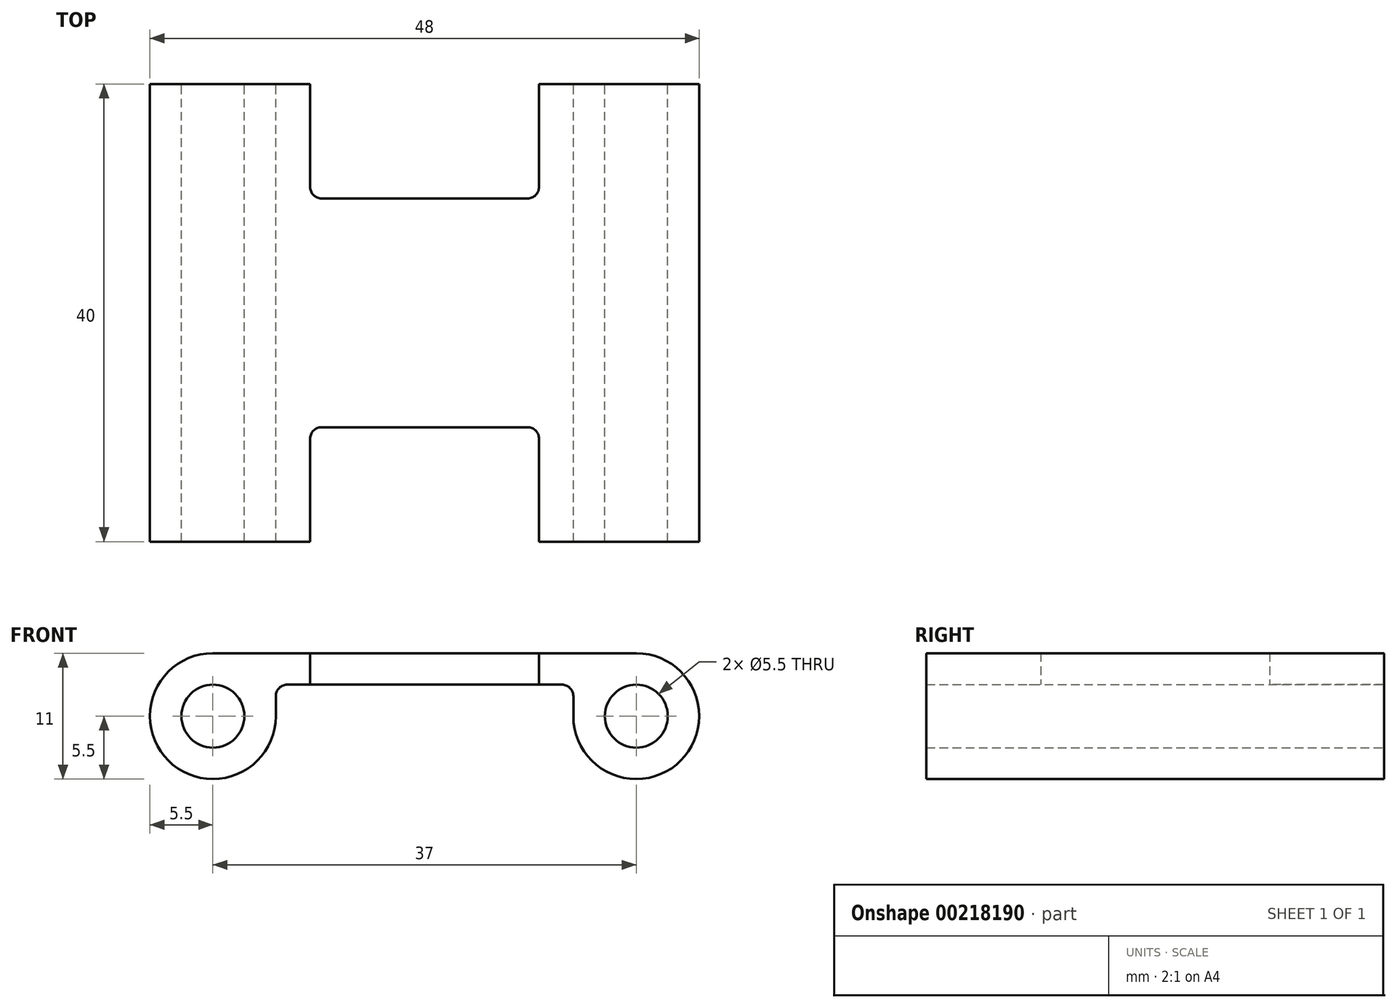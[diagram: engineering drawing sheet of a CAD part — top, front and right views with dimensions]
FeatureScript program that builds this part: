
annotation { "Feature Type Name" : "Feature", "Feature Type Description" : "" }
export const myFeature = defineFeature(function(context is Context, id is Id, definition is map)
    precondition{}
    {
        {
            var Q0;
            Q0=qCreatedBy(makeId("Front.planeOp"),FACE);
            var sketch = newSketch(context, id + "F0", { "sketchPlane" : qUnion([Q0])});
            skLineSegment(sketch, "E0", {"start": v(0, 5.5) * mm, "end": v(37, 5.5) * mm});
            skLineSegment(sketch, "E1", {"start": v(6.5, 2.75) * mm, "end": v(30.5, 2.75) * mm});
            skLineSegment(sketch, "E2", {"start": v(5.5, 0) * mm, "end": v(5.5, 1.75) * mm});
            skLineSegment(sketch, "E3", {"start": v(31.5, 0) * mm, "end": v(31.5, 1.75) * mm});
            skPoint(sketch, "E4.orphan", {"position": v(0, 2.75) * mm});
            skPoint(sketch, "E5.visualSharp", {"position": v(5.5, 2.75) * mm});
            skArc(sketch, "E5.filletArc", {"start": v(6.5, 2.75) * mm, "mid": v(5.8, 2.46) * mm, "end": v(5.5, 1.75) * mm});
            skPoint(sketch, "E6.visualSharp", {"position": v(31.5, 2.75) * mm});
            skArc(sketch, "E6.filletArc", {"start": v(31.5, 1.75) * mm, "mid": v(31.2, 2.46) * mm, "end": v(30.5, 2.75) * mm});
            skPoint(sketch, "E7.visualSharp", {"position": v(5.5, 0) * mm});
            skPoint(sketch, "E8.visualSharp", {"position": v(31.5, 0) * mm});
            skCircle(sketch, "E9", {"center": v(37, 0) * mm, "radius": 2.75 * mm});
            skCircle(sketch, "E10", {"center": v(0, 0) * mm, "radius": 2.75 * mm});
            skArc(sketch, "E11", {"start": v(31.5, 0) * mm, "mid": v(40.89, -3.89) * mm, "end": v(37, 5.5) * mm});
            skArc(sketch, "E12", {"start": v(0, 5.5) * mm, "mid": v(-3.89, -3.89) * mm, "end": v(5.5, 0) * mm});
            skSolve(sketch);
        }
        {
            var Q0;
            Q0=qSketchRegion(id+"F0",true);
            extrude(context, id + "F1", {"entities" : qUnion([Q0]), "depth" : 20 * mm, "hasSecondDirection" : true, "secondDirectionOppositeDirection" : true, "secondDirectionDepth" : 20 * mm});
        }
        {
            var Q0;
            {var subQ2=sQuery(id+"F0.wireOp",EDGE,"E1");Q0=makeQuery(id+"FyGTzeMTxIq73NX_1.boolean.opBoolean","SPLIT",FACE,{"disambiguationData":[TD([makeQuery(id+"FyGTzeMTxIq73NX_1.opExtrude","SWEPT_FACE",FACE,{"disambiguationData":[OSD([sQuery(id+"FarfYcdUMCQoenl_1.wireOp",EDGE,"kt06CgWY-HaNg-SO35-Ci6H-CknEjbLrrtwM.bottom")])]})])],"derivedFrom":makeQuery(id+"F1.opExtrude","SWEPT_FACE",FACE,{"disambiguationData":[OSD([subQ2])]})});}
            var sketch = newSketch(context, id + "F2", { "sketchPlane" : qUnion([Q0])});
            skLineSegment(sketch, "E13", {"start": v(18.5, -20) * mm, "end": v(18.5, 20.03) * mm, "construction": true});
            skLineSegment(sketch, "E14.bottom", {"start": v(8.5, -20) * mm, "end": v(28.5, -20) * mm});
            skLineSegment(sketch, "E14.top", {"start": v(8.5, -10) * mm, "end": v(28.5, -10) * mm});
            skLineSegment(sketch, "E14.left", {"start": v(8.5, -20) * mm, "end": v(8.5, -10) * mm});
            skLineSegment(sketch, "E14.right", {"start": v(28.5, -20) * mm, "end": v(28.5, -10) * mm});
            skLineSegment(sketch, "E15.bottom", {"start": v(8.5, 20) * mm, "end": v(28.5, 20) * mm});
            skLineSegment(sketch, "E15.top", {"start": v(8.5, 10) * mm, "end": v(28.5, 10) * mm});
            skLineSegment(sketch, "E15.left", {"start": v(8.5, 20) * mm, "end": v(8.5, 10) * mm});
            skLineSegment(sketch, "E15.right", {"start": v(28.5, 20) * mm, "end": v(28.5, 10) * mm});
            skLineSegment(sketch, "E16", {"start": v(-5.61, 0) * mm, "end": v(43.07, 0) * mm, "construction": true});
            skSolve(sketch);
        }
        {
            var Q0;
            Q0=qSketchRegion(id+"F2",true);
            extrude(context, id + "F3", {"entities" : qUnion([Q0]), "operationType" : NewBodyOperationType.REMOVE, "endBound" : BoundingType.UP_TO_NEXT, "oppositeDirection" : true, "depth" : 25 * mm});
        }
        {
            var Q0;
            Q0=makeQuery(id+"F3.boolean.opBoolean","COPY",EDGE,{"derivedFrom":makeQuery(id+"F3.opExtrude","CAP_EDGE",EDGE,{"disambiguationData":[OSD([sQuery(id+"F2.wireOp",EDGE,"E15.left")])],"isStart":true})});
            var Q1;
            Q1=makeQuery(id+"F3.boolean.opBoolean","COPY",EDGE,{"derivedFrom":makeQuery(id+"F3.opExtrude","CAP_EDGE",EDGE,{"disambiguationData":[OSD([sQuery(id+"F2.wireOp",EDGE,"E14.left")])],"isStart":true})});
            var Q2;
            Q2=makeQuery(id+"F3.boolean.opBoolean","COPY",EDGE,{"derivedFrom":makeQuery(id+"F3.opExtrude","CAP_EDGE",EDGE,{"disambiguationData":[OSD([sQuery(id+"F2.wireOp",EDGE,"E14.right")])],"isStart":true})});
            var Q3;
            Q3=makeQuery(id+"F3.boolean.opBoolean","COPY",EDGE,{"derivedFrom":makeQuery(id+"F3.opExtrude","CAP_EDGE",EDGE,{"disambiguationData":[OSD([sQuery(id+"F2.wireOp",EDGE,"E15.right")])],"isStart":true})});
            var Q4;
            Q4=makeQuery(id+"FyGTzeMTxIq73NX_1.opExtrude","CAP_EDGE",EDGE,{"disambiguationData":[OSD([sQuery(id+"FarfYcdUMCQoenl_1.wireOp",EDGE,"kt06CgWY-HaNg-SO35-Ci6H-CknEjbLrrtwM.top")])],"isStart":true});
            var Q5;
            Q5=makeQuery(id+"FyGTzeMTxIq73NX_1.opExtrude","CAP_EDGE",EDGE,{"disambiguationData":[OSD([sQuery(id+"FarfYcdUMCQoenl_1.wireOp",EDGE,"kt06CgWY-HaNg-SO35-Ci6H-CknEjbLrrtwM.bottom")])],"isStart":true});
            var Q6;
            Q6=makeQuery(id+"F3.boolean.opBoolean","COPY",EDGE,{"derivedFrom":makeQuery(id+"F3.opExtrude","SWEPT_EDGE",EDGE,{"disambiguationData":[OSD([sQuery(id+"F2.wireOp",EDGE,"E15.top"),sQuery(id+"F2.wireOp",EDGE,"E15.left")])]})});
            var Q7;
            Q7=makeQuery(id+"F3.boolean.opBoolean","COPY",EDGE,{"derivedFrom":makeQuery(id+"F3.opExtrude","SWEPT_EDGE",EDGE,{"disambiguationData":[OSD([sQuery(id+"F2.wireOp",EDGE,"E15.top"),sQuery(id+"F2.wireOp",EDGE,"E15.right")])]})});
            var Q8;
            Q8=makeQuery(id+"F3.boolean.opBoolean","COPY",EDGE,{"derivedFrom":makeQuery(id+"F3.opExtrude","SWEPT_EDGE",EDGE,{"disambiguationData":[OSD([sQuery(id+"F0.wireOp",EDGE,"E1"),sQuery(id+"FarfYcdUMCQoenl_1.wireOp",EDGE,"kt06CgWY-HaNg-SO35-Ci6H-CknEjbLrrtwM.bottom"),sQuery(id+"F2.wireOp",EDGE,"E14.top"),sQuery(id+"F2.wireOp",EDGE,"E14.right")])]})});
            var Q9;
            Q9=makeQuery(id+"F3.boolean.opBoolean","COPY",EDGE,{"derivedFrom":makeQuery(id+"F3.opExtrude","SWEPT_EDGE",EDGE,{"disambiguationData":[OSD([sQuery(id+"F0.wireOp",EDGE,"E1"),sQuery(id+"FarfYcdUMCQoenl_1.wireOp",EDGE,"kt06CgWY-HaNg-SO35-Ci6H-CknEjbLrrtwM.bottom"),sQuery(id+"F2.wireOp",EDGE,"E14.top"),sQuery(id+"F2.wireOp",EDGE,"E14.left")])]})});
            fillet(context, id + "F4", {"entities" : qUnion([Q0, Q1, Q2, Q3, Q4, Q5, Q6, Q7, Q8, Q9]), "radius" : 1 * mm, "tangentPropagation" : true, "allowEdgeOverflow" : false});
        }
    });
